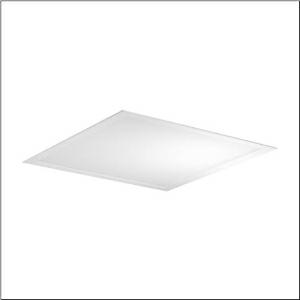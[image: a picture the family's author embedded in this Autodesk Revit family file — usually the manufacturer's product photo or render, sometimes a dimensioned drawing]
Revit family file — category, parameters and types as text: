
# Revit family: apollon_21_square_51mq11wd2414
name_source: partatom
category: Lighting Fixtures
units: mm (PartAtom-declared; Revit-internal decimal feet)

## family parameters
Cut with Voids When Loaded = No
Host = Face
Light Source = No
Part Type = Normal
Room Calculation Point = No
Round Connector Dimension = Use Diameter
Shared = No

## types (1)
- Apollon 21 square (1 x LED, 4200 lm, 24.7 W, 4000K)
    Apparent Load = 25 VA
    CIE Flux Codes = 60 87 97 100 100
    Color Rendering = 80
    Color Temperature = 4000K
    Default Elevation = 1800 mm
    Description = Apollon 21 square, office luminaire, primary optical cover: micro prismatic cover, of PMMA, CAT 2 (L<= 3000cd/m²), light emission: direct distribution, primary light characteristic: symmetric, installation type: lay-in mounting, LED, rated luminous flux: 4.200lm, luminous efficacy: 170lm/W, light colour: 840, colour temperature: 4000K, control gear: DALI 2, Multilumen, with terminal, 5-pole, mains connection: 220..240V, AC/DC, 0/50..60Hz, rated input power: 24.7W, housing, of aluminium, coated, traffic white (RAL 9016), module: M625, length: 620mm, width: 620mm, height: 55mm, recess depth: 180mm, housing upper side, of sheet steel, galvanised, protection rating (complete): IP20, protection rating (lamp compartment, on room side): IP50, insulation class (complete): insulation class II (safety insulation), certification: CE, ENEC, impact resistance: IK03, permissible operating ambient temperature: -20..+45°C, permissible storage temperature: -40..+80°C, standard: EN 60598-2-22, packaging unit: 1 piece
    Height = 0 mm  [stored 0 ft]
    Lamp = 1 x LED
    Lamp Light Flux = 4200 lm
    Lamp Power = 24.7 W
    Lamp count = 1
    Length = 620 mm
    Luminous efficacy = 170 lm/W
    Manufacturer = Siteco
    ModVariant = No
    Model = 51MQ11WD2414
    Mounting Place = Ceiling
    Mounting Type = Recessed
    Number of Poles = 1
    OnlyDefault = Yes
    Power Factor = 1
    Product Name = Apollon 21 square
    Product group = office luminaire | ceiling recessed
    ProductGroupID = 401
    Protection Class = Protection class II
    Protection Degree = IP 20
    RLX_Detail_Level = 1
    RLX_Emergency_Light_Flux = 0 lm
    RLX_Emergency_Type = 0
    RLX_Emergency_Type_DB = No
    RlxData = <blob elided: 13017 chars, md5=2bf32509>
    Socket = socket
    Standby Power = 0 W
    System Light Flux = 4200 lm
    System Power = 25 W
    Type Comments = Product without accessories
    Type Image = l_1291054.jpg
    URL = http://relux.com
    VarID = ---
    Voltage = 0 V
    Weight = 0.00 kg
    Width = 620 mm

note: [stored X ft] marks values corroborated as IEEE doubles in the binary element streams (Revit-internal decimal feet)

## geometry (parser evidence)
native form markers: Sweep x9
no freeform markers — native parametric forms only
